# Revit family: 63_UN_LF_Power Stripelite 9_LI
name_source: partatom
category: Lighting Fixtures
units: mm (PartAtom-declared; Revit-internal decimal feet)

## family parameters
Always vertical = Yes
Cut with Voids When Loaded = No
Light Source = Yes
OmniClass Number = 23.80.70.11.14.11
OmniClass Title = Downlights
Part Type = Normal
Room Calculation Point = Yes
Round Connector Dimension = Use Diameter
Shared = No
Work Plane-Based = No

## types (1)
- Power Stripelite 9 opaal
    Apparent Load = 12 VA
    Assembly Code = 63.0
    Calc_L1_Symbol = 9 mm  [stored 0.0295276 ft]
    Calc_L2_Symbol = 1 mm  [stored 0.00328084 ft]
    Color Filter = 16777215
    Description = DALI | 1-10V
    Dimming Lamp Color Temperature Shift = <None>
    ETIM Code = ETIMCODE
    Emit Shape Visible in Rendering = No
    Emit from Rectangle Length = 915 mm  [stored 3.00197 ft]
    Emit from Rectangle Width = 55 mm  [stored 0.180446 ft]
    GTIN Code = GTINCODE
    H1 = 65 mm  [stored 0.213255 ft]
    Housing_Material = Select RGB Value for different appearance
    IK Value = IK16
    IP Value = IP65
    ISBN Code = ISBNCODE
    IfcExportAs = IfcLightFixtureType
    IfcExportType = USERDEFINED
    L1 = 925 mm  [stored 3.03478 ft]
    L2 = 65 mm  [stored 0.213255 ft]
    L3 = 5 mm  [stored 0.0164042 ft]
    Lamp = LED
    Luminous Flux (lm) = 1920 lm
    Manufacturer = Light International
    Model = Power Stripelite
    Photometric Web File = PSL9_O_LDT.ies
    Tilt Angle = 90.00°
    Type Comments = Power Stripelite 9
    URL = https://lightinternational.nl
    Voltage = 230 V
    Wattage Comments = 12

note: [stored X ft] marks values corroborated as IEEE doubles in the binary element streams (Revit-internal decimal feet)

## geometry (parser evidence)
native form markers: Sweep x7
no freeform markers — native parametric forms only
